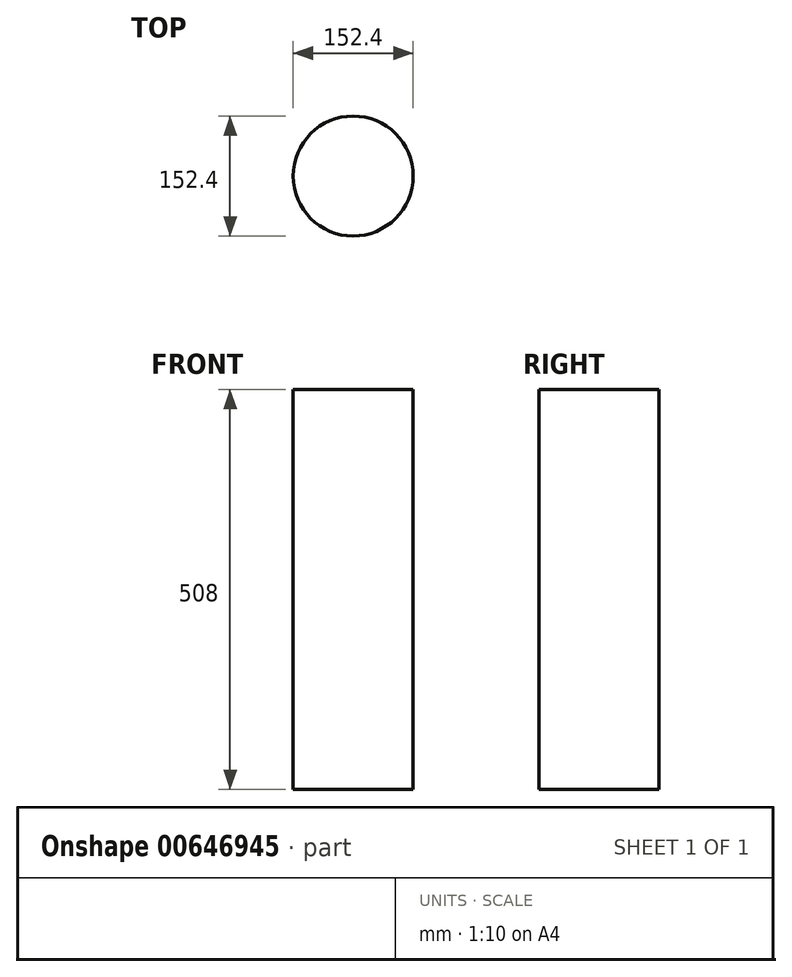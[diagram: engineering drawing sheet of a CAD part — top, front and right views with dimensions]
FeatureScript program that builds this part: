
annotation { "Feature Type Name" : "Feature", "Feature Type Description" : "" }
export const myFeature = defineFeature(function(context is Context, id is Id, definition is map)
    precondition{}
    {
        {
            var Q0;
            Q0=qCreatedBy(makeId("Top.planeOp"),FACE);
            var sketch = newSketch(context, id + "F0", { "sketchPlane" : qUnion([Q0])});
            skCircle(sketch, "E0", {"center": v(0, 0) * mm, "radius": 76.2 * mm});
            skSolve(sketch);
        }
        {
            var Q0;
            Q0=makeQuery(id+"F0.imprint","IMPRINT",FACE,{"disambiguationData":[TD([[makeQuery(id+"F0.imprint","IMPRINT",EDGE,{"derivedFrom":sQuery(id+"F0.wireOp",EDGE,"E0")}),1.0]])]});
            extrude(context, id + "F1", {"entities" : qUnion([Q0]), "depth" : 508 * mm, "offsetDistance" : 25.4 * mm});
        }
    });
